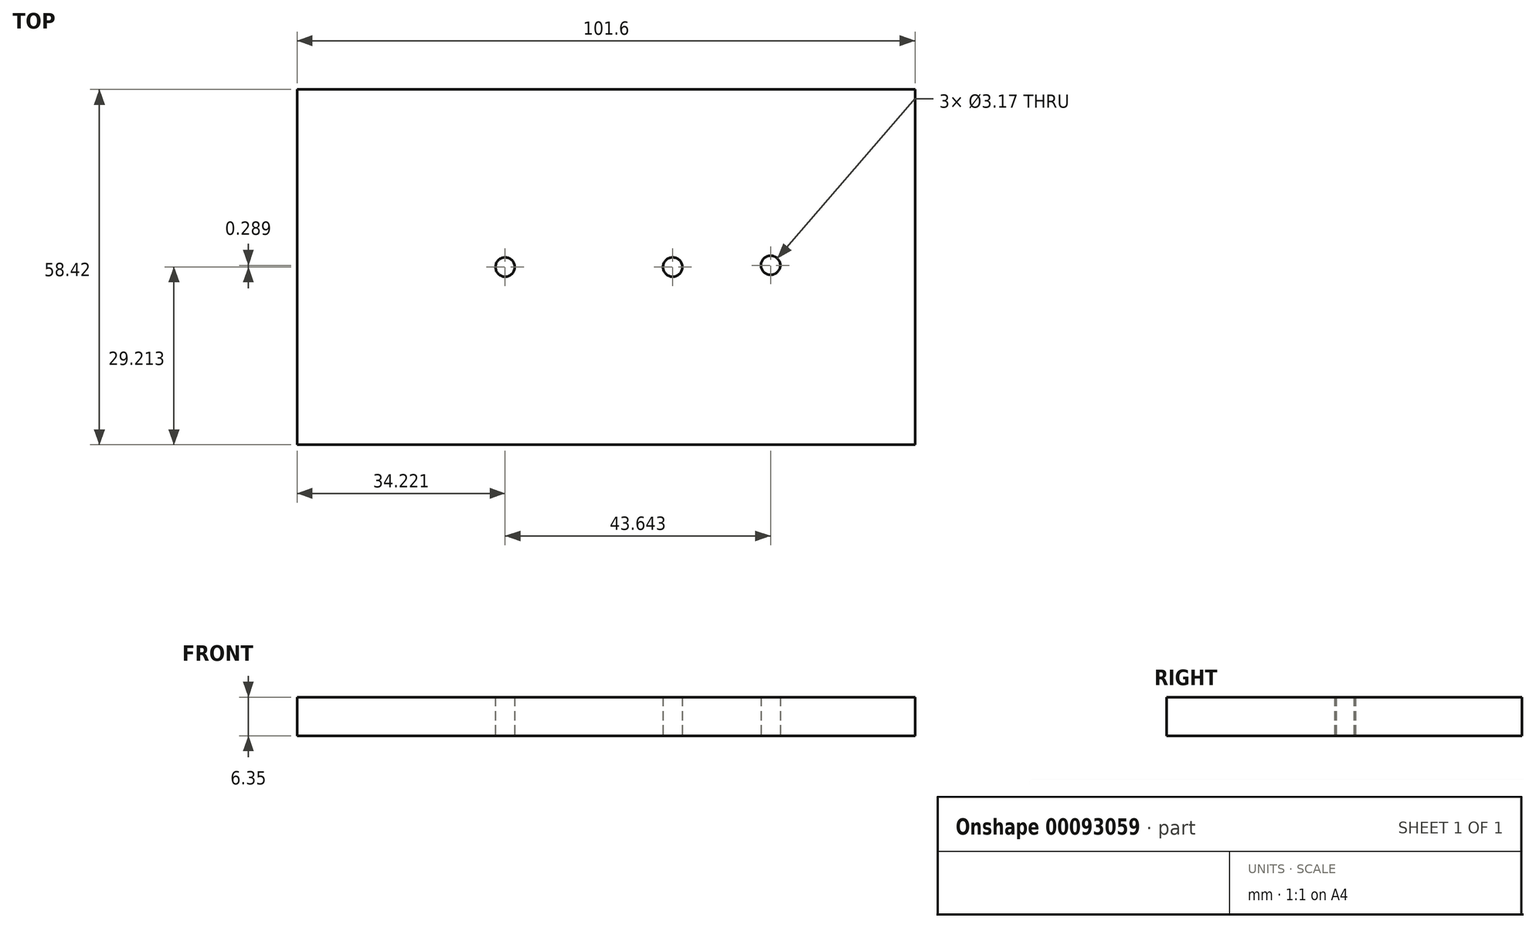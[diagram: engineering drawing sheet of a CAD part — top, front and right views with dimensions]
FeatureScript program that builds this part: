
annotation { "Feature Type Name" : "Feature", "Feature Type Description" : "" }
export const myFeature = defineFeature(function(context is Context, id is Id, definition is map)
    precondition{}
    {
        {
            var Q0;
            Q0=qCreatedBy(makeId("Top.planeOp"),FACE);
            var sketch = newSketch(context, id + "F0", { "sketchPlane" : qUnion([Q0])});
            skCircle(sketch, "E0", {"center": v(-21.02, -3.56) * mm, "radius": 19.05 * mm});
            skCircle(sketch, "E1", {"center": v(6.53, -3.56) * mm, "radius": 8.5 * mm});
            skLineSegment(sketch, "E2.bottom", {"start": v(-55.24, 25.65) * mm, "end": v(46.36, 25.65) * mm});
            skLineSegment(sketch, "E2.top", {"start": v(-55.24, -32.77) * mm, "end": v(46.36, -32.77) * mm});
            skLineSegment(sketch, "E2.left", {"start": v(-55.24, 25.65) * mm, "end": v(-55.24, -32.77) * mm});
            skLineSegment(sketch, "E2.right", {"start": v(46.36, 25.65) * mm, "end": v(46.36, -32.77) * mm});
            skCircle(sketch, "E3", {"center": v(22.62, -3.27) * mm, "radius": 7.15 * mm});
            skLineSegment(sketch, "E4", {"start": v(46.36, -3.56) * mm, "end": v(-55.24, -3.56) * mm});
            skLineSegment(sketch, "E5", {"start": v(-21.02, -3.56) * mm, "end": v(-21.02, 25.65) * mm});
            skLineSegment(sketch, "E6", {"start": v(6.53, -3.56) * mm, "end": v(6.53, 25.65) * mm});
            skLineSegment(sketch, "E7", {"start": v(22.62, -3.27) * mm, "end": v(22.62, 25.65) * mm});
            skCircle(sketch, "E8", {"center": v(-21.02, -3.56) * mm, "radius": 1.59 * mm});
            skCircle(sketch, "E9", {"center": v(6.53, -3.56) * mm, "radius": 1.59 * mm});
            skCircle(sketch, "E10", {"center": v(22.62, -3.27) * mm, "radius": 1.59 * mm});
            skSolve(sketch);
        }
        {
            var Q0;
            {var subQ0=sQuery(id+"F0.wireOp",EDGE,"E7");var subQ1=sQuery(id+"F0.wireOp",EDGE,"E3");var subQ2=makeQuery(id+"F0.imprint","INTERSECT",VERTEX,{"derivedFrom":[subQ1,subQ0]});Q0=makeQuery(id+"F0.imprint","IMPRINT",FACE,{"disambiguationData":[TD([[makeQuery(id+"F0.imprint","IMPRINT",EDGE,{"disambiguationData":[TD([[subQ2,-1.0]])],"derivedFrom":subQ1}),1.0]])]});}
            var Q1;
            {var subQ0=sQuery(id+"F0.wireOp",EDGE,"E4");var subQ1=sQuery(id+"F0.wireOp",EDGE,"E1");var subQ2=makeQuery(id+"F0.imprint","INTERSECT",VERTEX,{"derivedFrom":[subQ1,subQ0]});Q1=makeQuery(id+"F0.imprint","IMPRINT",FACE,{"disambiguationData":[TD([[makeQuery(id+"F0.imprint","IMPRINT",EDGE,{"disambiguationData":[TD([[subQ2,-1.0]])],"derivedFrom":subQ0}),1.0]])]});}
            var Q2;
            {var subQ1=sQuery(id+"F0.wireOp",EDGE,"E2.top");Q2=makeQuery(id+"F0.imprint","IMPRINT",FACE,{"disambiguationData":[TD([[makeQuery(id+"F0.imprint","IMPRINT",EDGE,{"derivedFrom":subQ1}),1.0]])]});}
            var Q3;
            {var subQ0=sQuery(id+"F0.wireOp",EDGE,"E4");var subQ1=sQuery(id+"F0.wireOp",EDGE,"E3");var subQ2=makeQuery(id+"F0.imprint","INTERSECT",VERTEX,{"disambiguationData":[OD(0.0)],"derivedFrom":[subQ1,subQ0]});Q3=makeQuery(id+"F0.imprint","IMPRINT",FACE,{"disambiguationData":[TD([[makeQuery(id+"F0.imprint","IMPRINT",EDGE,{"disambiguationData":[TD([[subQ2,1.0]])],"derivedFrom":subQ1}),1.0]])]});}
            var Q4;
            {var subQ0=sQuery(id+"F0.wireOp",EDGE,"E6");var subQ1=sQuery(id+"F0.wireOp",EDGE,"E1");var subQ2=makeQuery(id+"F0.imprint","INTERSECT",VERTEX,{"derivedFrom":[subQ1,subQ0]});Q4=makeQuery(id+"F0.imprint","IMPRINT",FACE,{"disambiguationData":[TD([[makeQuery(id+"F0.imprint","IMPRINT",EDGE,{"disambiguationData":[TD([[subQ2,1.0]])],"derivedFrom":subQ1}),1.0]])]});}
            var Q5;
            {var subQ0=sQuery(id+"F0.wireOp",EDGE,"E7");var subQ1=sQuery(id+"F0.wireOp",EDGE,"E3");var subQ2=makeQuery(id+"F0.imprint","INTERSECT",VERTEX,{"derivedFrom":[subQ1,subQ0]});Q5=makeQuery(id+"F0.imprint","IMPRINT",FACE,{"disambiguationData":[TD([[makeQuery(id+"F0.imprint","IMPRINT",EDGE,{"disambiguationData":[TD([[subQ2,1.0]])],"derivedFrom":subQ1}),1.0]])]});}
            var Q6;
            {var subQ0=sQuery(id+"F0.wireOp",EDGE,"E5");var subQ1=sQuery(id+"F0.wireOp",EDGE,"E0");var subQ2=makeQuery(id+"F0.imprint","INTERSECT",VERTEX,{"derivedFrom":[subQ1,subQ0]});Q6=makeQuery(id+"F0.imprint","IMPRINT",FACE,{"disambiguationData":[TD([[makeQuery(id+"F0.imprint","IMPRINT",EDGE,{"disambiguationData":[TD([[subQ2,-1.0]])],"derivedFrom":subQ1}),1.0]])]});}
            var Q7;
            {var subQ0=sQuery(id+"F0.wireOp",EDGE,"E4");var subQ1=sQuery(id+"F0.wireOp",EDGE,"E0");var subQ2=makeQuery(id+"F0.imprint","INTERSECT",VERTEX,{"derivedFrom":[subQ1,subQ0]});Q7=makeQuery(id+"F0.imprint","IMPRINT",FACE,{"disambiguationData":[TD([[makeQuery(id+"F0.imprint","IMPRINT",EDGE,{"disambiguationData":[TD([[subQ2,1.0]])],"derivedFrom":subQ0}),1.0]])]});}
            var Q8;
            {var subQ5=sQuery(id+"F0.wireOp",EDGE,"E5");var subQ7=sQuery(id+"F0.wireOp",EDGE,"E0");var subQ9=makeQuery(id+"F0.imprint","INTERSECT",VERTEX,{"derivedFrom":[subQ7,subQ5]});Q8=makeQuery(id+"F0.imprint","IMPRINT",FACE,{"disambiguationData":[TD([[makeQuery(id+"F0.imprint","IMPRINT",EDGE,{"disambiguationData":[TD([[subQ9,-1.0]])],"derivedFrom":subQ7}),-1.0]])]});}
            var Q9;
            {var subQ1=sQuery(id+"F0.wireOp",EDGE,"E2.right");var subQ7=sQuery(id+"F0.wireOp",EDGE,"E2.bottom");var subQ8=makeQuery(id+"F0.imprint","INTERSECT",VERTEX,{"derivedFrom":[subQ7,subQ1]});Q9=makeQuery(id+"F0.imprint","IMPRINT",FACE,{"disambiguationData":[TD([[makeQuery(id+"F0.imprint","IMPRINT",EDGE,{"disambiguationData":[TD([[subQ8,1.0]])],"derivedFrom":subQ7}),-1.0]])]});}
            var Q10;
            {var subQ0=sQuery(id+"F0.wireOp",EDGE,"E5");var subQ1=sQuery(id+"F0.wireOp",EDGE,"E2.bottom");var subQ2=makeQuery(id+"F0.imprint","INTERSECT",VERTEX,{"derivedFrom":[subQ1,subQ0]});Q10=makeQuery(id+"F0.imprint","IMPRINT",FACE,{"disambiguationData":[TD([[makeQuery(id+"F0.imprint","IMPRINT",EDGE,{"disambiguationData":[TD([[subQ2,-1.0]])],"derivedFrom":subQ1}),-1.0]])]});}
            var Q11;
            {var subQ0=sQuery(id+"F0.wireOp",EDGE,"E5");var subQ1=sQuery(id+"F0.wireOp",EDGE,"E0");var subQ2=makeQuery(id+"F0.imprint","INTERSECT",VERTEX,{"derivedFrom":[subQ1,subQ0]});Q11=makeQuery(id+"F0.imprint","IMPRINT",FACE,{"disambiguationData":[TD([[makeQuery(id+"F0.imprint","IMPRINT",EDGE,{"disambiguationData":[TD([[subQ2,1.0]])],"derivedFrom":subQ0}),-1.0]])]});}
            var Q12;
            {var subQ0=sQuery(id+"F0.wireOp",EDGE,"E6");var subQ6=sQuery(id+"F0.wireOp",EDGE,"E1");var subQ11=makeQuery(id+"F0.imprint","INTERSECT",VERTEX,{"derivedFrom":[subQ6,subQ0]});Q12=makeQuery(id+"F0.imprint","IMPRINT",FACE,{"disambiguationData":[TD([[makeQuery(id+"F0.imprint","IMPRINT",EDGE,{"disambiguationData":[TD([[subQ11,1.0]])],"derivedFrom":subQ6}),-1.0]])]});}
            var Q13;
            {var subQ0=sQuery(id+"F0.wireOp",EDGE,"E6");var subQ1=sQuery(id+"F0.wireOp",EDGE,"E1");var subQ2=makeQuery(id+"F0.imprint","INTERSECT",VERTEX,{"derivedFrom":[subQ1,subQ0]});Q13=makeQuery(id+"F0.imprint","IMPRINT",FACE,{"disambiguationData":[TD([[makeQuery(id+"F0.imprint","IMPRINT",EDGE,{"disambiguationData":[TD([[subQ2,1.0]])],"derivedFrom":subQ0}),1.0]])]});}
            var Q14;
            {var subQ0=sQuery(id+"F0.wireOp",EDGE,"E4");var subQ1=sQuery(id+"F0.wireOp",EDGE,"E3");var subQ2=makeQuery(id+"F0.imprint","INTERSECT",VERTEX,{"disambiguationData":[OD(0.0)],"derivedFrom":[subQ1,subQ0]});Q14=makeQuery(id+"F0.imprint","IMPRINT",FACE,{"disambiguationData":[TD([[makeQuery(id+"F0.imprint","IMPRINT",EDGE,{"disambiguationData":[TD([[subQ2,-1.0]])],"derivedFrom":subQ1}),1.0]])]});}
            extrude(context, id + "F1", {"entities" : qUnion([Q0, Q1, Q2, Q3, Q4, Q5, Q6, Q7, Q8, Q9, Q10, Q11, Q12, Q13, Q14]), "depth" : 6.35 * mm});
        }
    });
